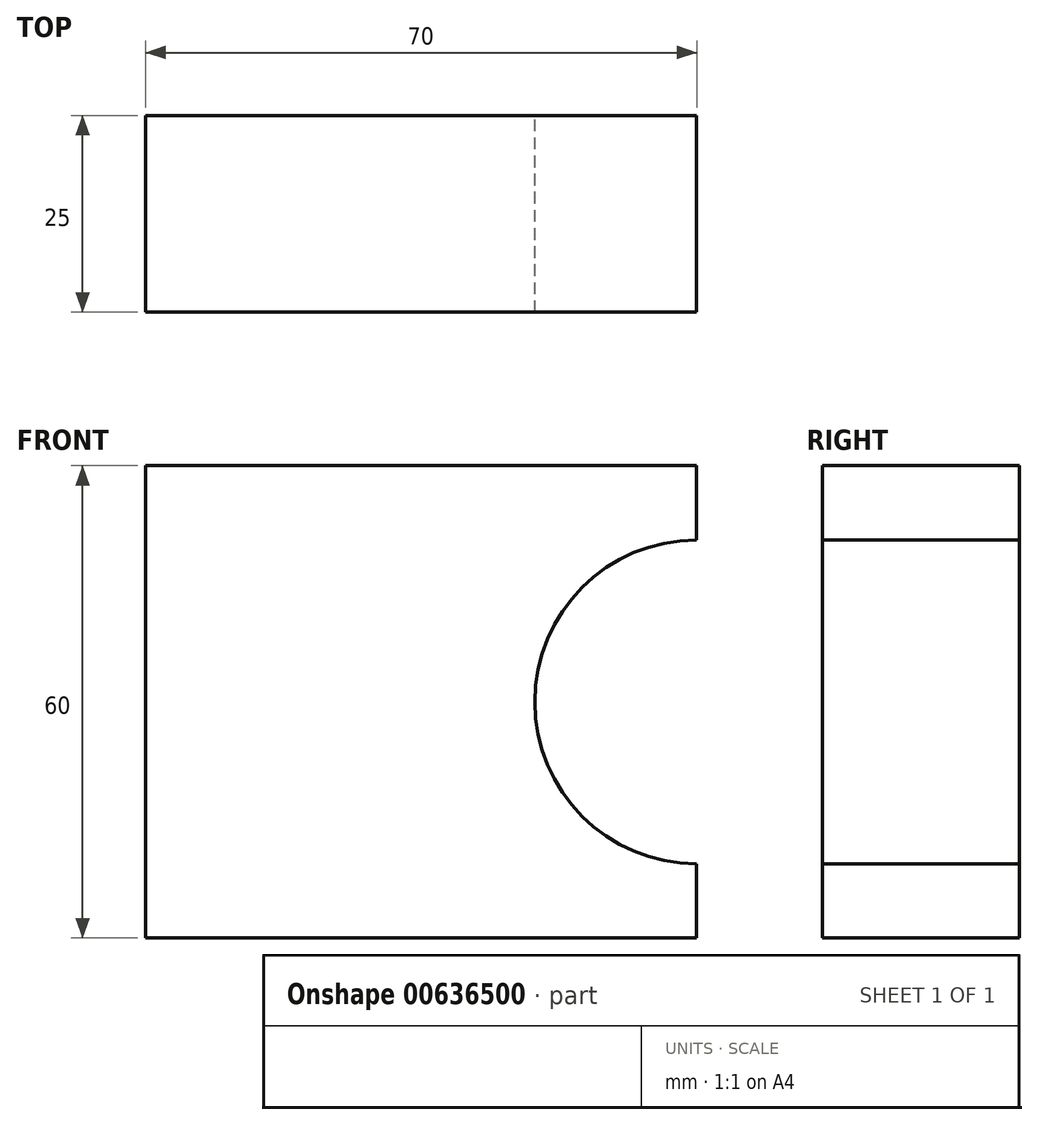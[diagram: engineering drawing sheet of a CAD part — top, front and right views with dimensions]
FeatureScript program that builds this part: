
annotation { "Feature Type Name" : "Feature", "Feature Type Description" : "" }
export const myFeature = defineFeature(function(context is Context, id is Id, definition is map)
    precondition{}
    {
        {
            var Q0;
            Q0=qCreatedBy(makeId("Front.planeOp"),FACE);
            var sketch = newSketch(context, id + "F0", { "sketchPlane" : qUnion([Q0])});
            skLineSegment(sketch, "E0.bottom", {"start": v(-46.95, 64.66) * mm, "end": v(23.05, 64.66) * mm});
            skLineSegment(sketch, "E0.top", {"start": v(-46.95, 4.66) * mm, "end": v(23.05, 4.66) * mm});
            skLineSegment(sketch, "E0.left", {"start": v(-46.95, 64.66) * mm, "end": v(-46.95, 4.66) * mm});
            skLineSegment(sketch, "E0.right", {"start": v(23.05, 64.66) * mm, "end": v(23.05, 4.66) * mm});
            skCircle(sketch, "E1", {"center": v(23.05, 34.66) * mm, "radius": 20.56 * mm});
            skSolve(sketch);
        }
        {
            var Q0;
            {var subQ1=sQuery(id+"F0.wireOp",EDGE,"E0.bottom");Q0=makeQuery(id+"F0.imprint","IMPRINT",FACE,{"disambiguationData":[TD([[makeQuery(id+"F0.imprint","IMPRINT",EDGE,{"derivedFrom":subQ1}),-1.0]])]});}
            extrude(context, id + "F1", {"entities" : qUnion([Q0]), "depth" : 25 * mm, "offsetDistance" : 25 * mm});
        }
    });
